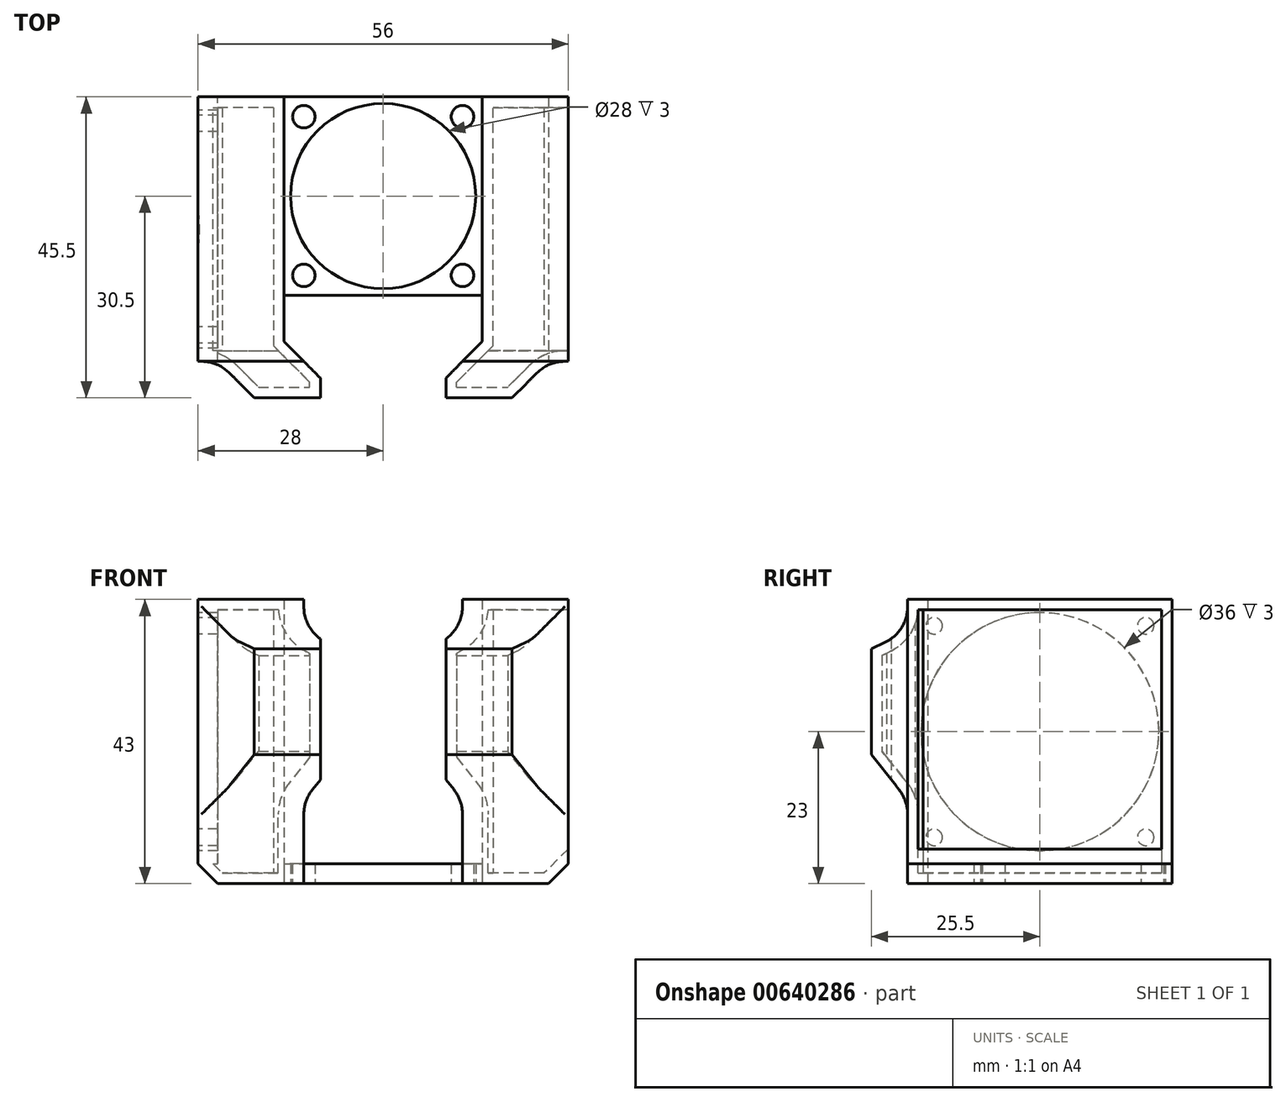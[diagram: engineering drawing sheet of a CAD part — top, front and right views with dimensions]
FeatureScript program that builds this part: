
annotation { "Feature Type Name" : "Feature", "Feature Type Description" : "" }
export const myFeature = defineFeature(function(context is Context, id is Id, definition is map)
    precondition{}
    {
        {
            var Q0;
            Q0=qCreatedBy(makeId("Top.planeOp"),FACE);
            var sketch = newSketch(context, id + "F0", { "sketchPlane" : qUnion([Q0])});
            skLineSegment(sketch, "E0", {"start": v(0, 0) * mm, "end": v(15, 0) * mm});
            skLineSegment(sketch, "E1", {"start": v(15, 0) * mm, "end": v(15, 30) * mm});
            skLineSegment(sketch, "E2", {"start": v(15, 30) * mm, "end": v(-15, 30) * mm});
            skLineSegment(sketch, "E3", {"start": v(-15, 30) * mm, "end": v(-15, 0) * mm});
            skLineSegment(sketch, "E4", {"start": v(-15, 0) * mm, "end": v(0, 0) * mm});
            skLineSegment(sketch, "E5", {"start": v(0, 0) * mm, "end": v(0, -15.5) * mm, "construction": true});
            skLineSegment(sketch, "E6", {"start": v(0, -15.5) * mm, "end": v(7, -15.5) * mm, "construction": true});
            skLineSegment(sketch, "E7", {"start": v(7, -15.5) * mm, "end": v(7, 0) * mm, "construction": true});
            skLineSegment(sketch, "E8", {"start": v(0, -15.5) * mm, "end": v(-7, -15.5) * mm, "construction": true});
            skLineSegment(sketch, "E9", {"start": v(-7, -15.5) * mm, "end": v(-7, 0) * mm, "construction": true});
            skLineSegment(sketch, "E10", {"start": v(-7, -15.5) * mm, "end": v(-47, -15.5) * mm, "construction": true});
            skLineSegment(sketch, "E11", {"start": v(7, -15.5) * mm, "end": v(47, -15.5) * mm, "construction": true});
            skLineSegment(sketch, "E12", {"start": v(-15, 30) * mm, "end": v(-15, -10) * mm, "construction": true});
            skLineSegment(sketch, "E13", {"start": v(15, 30) * mm, "end": v(15, -10) * mm, "construction": true});
            skLineSegment(sketch, "E14", {"start": v(-15, 30) * mm, "end": v(-25, 30) * mm});
            skLineSegment(sketch, "E15", {"start": v(-25, 30) * mm, "end": v(-25, -10) * mm, "construction": true});
            skLineSegment(sketch, "E16", {"start": v(-25, 30) * mm, "end": v(-28, 30) * mm});
            skLineSegment(sketch, "E17", {"start": v(-28, 30) * mm, "end": v(-28, -10) * mm});
            skLineSegment(sketch, "E18", {"start": v(-28, -10) * mm, "end": v(-25, -10) * mm});
            skLineSegment(sketch, "E19", {"start": v(-25, -10) * mm, "end": v(-19.5, -15.5) * mm});
            skLineSegment(sketch, "E20", {"start": v(-15, 0) * mm, "end": v(-15, -10) * mm});
            skLineSegment(sketch, "E21", {"start": v(-19.5, -15.5) * mm, "end": v(-9.5, -15.5) * mm});
            skLineSegment(sketch, "E22.MirrorCS", {"start": v(28, 30) * mm, "end": v(28, -10) * mm});
            skLineSegment(sketch, "E23.MirrorCS", {"start": v(28, -10) * mm, "end": v(25, -10) * mm});
            skLineSegment(sketch, "E24.MirrorCS", {"start": v(25, -10) * mm, "end": v(19.5, -15.5) * mm});
            skLineSegment(sketch, "E25.MirrorCS", {"start": v(15, 30) * mm, "end": v(25, 30) * mm});
            skLineSegment(sketch, "E26.MirrorCS", {"start": v(25, 30) * mm, "end": v(28, 30) * mm});
            skLineSegment(sketch, "E27", {"start": v(15, 0) * mm, "end": v(15, -10) * mm});
            skLineSegment(sketch, "E28", {"start": v(9.5, -15.5) * mm, "end": v(19.5, -15.5) * mm});
            skLineSegment(sketch, "E29", {"start": v(0, 30) * mm, "end": v(0, 0) * mm});
            skCircle(sketch, "E30", {"center": v(0, 15) * mm, "radius": 14 * mm});
            skLineSegment(sketch, "E31", {"start": v(-12, 27) * mm, "end": v(-12, 3) * mm, "construction": true});
            skLineSegment(sketch, "E32", {"start": v(-12, 3) * mm, "end": v(12, 3) * mm, "construction": true});
            skLineSegment(sketch, "E33", {"start": v(12, 3) * mm, "end": v(-12, 27) * mm, "construction": true});
            skLineSegment(sketch, "E34", {"start": v(-12, 27) * mm, "end": v(12, 27) * mm, "construction": true});
            skLineSegment(sketch, "E35", {"start": v(12, 27) * mm, "end": v(12, 3) * mm, "construction": true});
            skCircle(sketch, "E36", {"center": v(-12, 27) * mm, "radius": 1.7 * mm});
            skCircle(sketch, "E37", {"center": v(12, 27) * mm, "radius": 1.7 * mm});
            skCircle(sketch, "E38", {"center": v(12, 3) * mm, "radius": 1.7 * mm});
            skCircle(sketch, "E39", {"center": v(-12, 3) * mm, "radius": 1.7 * mm});
            skLineSegment(sketch, "E40", {"start": v(-9.5, -15.5) * mm, "end": v(-9.5, -12.5) * mm});
            skLineSegment(sketch, "E41", {"start": v(-9.5, -12.5) * mm, "end": v(-15, -7) * mm});
            skLineSegment(sketch, "E42.MirrorCS", {"start": v(9.5, -15.5) * mm, "end": v(9.5, -12.5) * mm});
            skLineSegment(sketch, "E43.MirrorCS", {"start": v(9.5, -12.5) * mm, "end": v(15, -7) * mm});
            skSolve(sketch);
        }
        {
            var Q0;
            {var subQ6=sQuery(id+"F0.wireOp",EDGE,"E3");Q0=makeQuery(id+"F0.imprint","IMPRINT",FACE,{"disambiguationData":[TD([[makeQuery(id+"F0.imprint","IMPRINT",EDGE,{"derivedFrom":subQ6}),1.0]])]});}
            var Q1;
            {var subQ5=sQuery(id+"F0.wireOp",EDGE,"E0");Q1=makeQuery(id+"F0.imprint","IMPRINT",FACE,{"disambiguationData":[TD([[makeQuery(id+"F0.imprint","IMPRINT",EDGE,{"derivedFrom":subQ5}),1.0]])]});}
            extrude(context, id + "F1", {"entities" : qUnion([Q0, Q1]), "depth" : 3 * mm, "offsetDistance" : 25 * mm});
        }
        {
            var Q0;
            Q0=makeQuery(id+"F0.imprint","IMPRINT",FACE,{"disambiguationData":[TD([[makeQuery(id+"F0.imprint","IMPRINT",EDGE,{"derivedFrom":sQuery(id+"F0.wireOp",EDGE,"E3")}),-1.0]])]});
            var Q1;
            Q1=makeQuery(id+"F0.imprint","IMPRINT",FACE,{"disambiguationData":[TD([[makeQuery(id+"F0.imprint","IMPRINT",EDGE,{"derivedFrom":sQuery(id+"F0.wireOp",EDGE,"E1")}),-1.0]])]});
            extrude(context, id + "F2", {"entities" : qUnion([Q0, Q1]), "operationType" : NewBodyOperationType.ADD, "depth" : 43 * mm, "offsetDistance" : 25 * mm});
        }
        {
            var Q0;
            Q0=qCreatedBy(makeId("Right.planeOp"),FACE);
            var sketch = newSketch(context, id + "F3", { "sketchPlane" : qUnion([Q0])});
            skLineSegment(sketch, "E44.0", {"start": v(-15.5, 19.5) * mm, "end": v(-15.5, 0) * mm});
            skLineSegment(sketch, "E45", {"start": v(-10, 12.58) * mm, "end": v(-15.5, 19.5) * mm});
            skLineSegment(sketch, "E46", {"start": v(0, 0) * mm, "end": v(-15.5, 0) * mm});
            skPoint(sketch, "E47.orphan", {"position": v(-15.5, 43) * mm});
            skLineSegment(sketch, "E48", {"start": v(-15.5, 43) * mm, "end": v(-15.5, 27.5) * mm});
            skLineSegment(sketch, "E49", {"start": v(-15.5, 43) * mm, "end": v(0, 43) * mm});
            skLineSegment(sketch, "E50", {"start": v(-10, 38.16) * mm, "end": v(-15.5, 35.5) * mm});
            skLineSegment(sketch, "E51.0", {"start": v(-10, 43) * mm, "end": v(-10, 0) * mm});
            skSolve(sketch);
        }
        {
            var Q0;
            Q0 = qSketchRegion(id + "F3", true);
            extrude(context, id + "F4", {"entities" : qUnion([Q0]), "operationType" : NewBodyOperationType.REMOVE, "oppositeDirection" : true, "depth" : 25 * mm, "offsetDistance" : 25 * mm, "hasSecondDirection" : true, "secondDirectionOppositeDirection" : false, "secondDirectionDepth" : 25 * mm});
        }
        {
            var Q0;
            {var subQ0=sQuery(id+"F3.wireOp",EDGE,"E50");var subQ1=sQuery(id+"F3.wireOp",EDGE,"E51.0");Q0=makeQuery(id+"F4.boolean.opBoolean","COPY",EDGE,{"disambiguationData":[topologyDisambiguationEdgeConnected([makeQuery(id+"F2.opExtrude","SWEPT_FACE",FACE,{"disambiguationData":[OSD([sQuery(id+"F0.wireOp",EDGE,"E18")])]})])],"derivedFrom":makeQuery(id+"F4.opExtrude","SWEPT_EDGE",EDGE,{"disambiguationData":[OSD([subQ0,subQ1])]})});}
            var Q1;
            Q1=makeQuery(id+"F2.opExtrude","SWEPT_EDGE",EDGE,{"disambiguationData":[OSD([sQuery(id+"F0.wireOp",EDGE,"E18"),sQuery(id+"F0.wireOp",EDGE,"E19")])]});
            var Q2;
            {var subQ0=sQuery(id+"F3.wireOp",EDGE,"E45");var subQ1=sQuery(id+"F3.wireOp",EDGE,"E51.0");Q2=makeQuery(id+"F4.boolean.opBoolean","COPY",EDGE,{"disambiguationData":[topologyDisambiguationEdgeConnected([makeQuery(id+"F2.opExtrude","SWEPT_FACE",FACE,{"disambiguationData":[OSD([sQuery(id+"F0.wireOp",EDGE,"E18")])]})])],"derivedFrom":makeQuery(id+"F4.opExtrude","SWEPT_EDGE",EDGE,{"disambiguationData":[OSD([subQ0,subQ1])]})});}
            var Q3;
            {var subQ0=sQuery(id+"F3.wireOp",EDGE,"E45");var subQ1=sQuery(id+"F3.wireOp",EDGE,"E51.0");Q3=makeQuery(id+"F4.boolean.opBoolean","COPY",EDGE,{"disambiguationData":[topologyDisambiguationEdgeConnected([makeQuery(id+"F2.opExtrude","SWEPT_FACE",FACE,{"disambiguationData":[OSD([sQuery(id+"F0.wireOp",EDGE,"E23.MirrorCS")])]})])],"derivedFrom":makeQuery(id+"F4.opExtrude","SWEPT_EDGE",EDGE,{"disambiguationData":[OSD([subQ0,subQ1])]})});}
            var Q4;
            Q4=makeQuery(id+"F2.opExtrude","SWEPT_EDGE",EDGE,{"disambiguationData":[OSD([sQuery(id+"F0.wireOp",EDGE,"E23.MirrorCS"),sQuery(id+"F0.wireOp",EDGE,"E24.MirrorCS")])]});
            var Q5;
            {var subQ0=sQuery(id+"F3.wireOp",EDGE,"E50");var subQ1=sQuery(id+"F3.wireOp",EDGE,"E51.0");Q5=makeQuery(id+"F4.boolean.opBoolean","COPY",EDGE,{"disambiguationData":[topologyDisambiguationEdgeConnected([makeQuery(id+"F2.opExtrude","SWEPT_FACE",FACE,{"disambiguationData":[OSD([sQuery(id+"F0.wireOp",EDGE,"E23.MirrorCS")])]})])],"derivedFrom":makeQuery(id+"F4.opExtrude","SWEPT_EDGE",EDGE,{"disambiguationData":[OSD([subQ0,subQ1])]})});}
            fillet(context, id + "F5", {"entities" : qUnion([Q0, Q1, Q2, Q3, Q4, Q5]), "radius" : 6 * mm, "tangentPropagation" : true, "allowEdgeOverflow" : false});
        }
        {
            var Q0;
            Q0=makeQuery(id+"F2.opExtrude","CAP_EDGE",EDGE,{"disambiguationData":[OSD([sQuery(id+"F0.wireOp",EDGE,"E22.MirrorCS")])],"isStart":true});
            var Q1;
            Q1=makeQuery(id+"F2.opExtrude","CAP_EDGE",EDGE,{"disambiguationData":[OSD([sQuery(id+"F0.wireOp",EDGE,"E17")])],"isStart":true});
            chamfer(context, id + "F6", {"entities" : qUnion([Q0, Q1]), "width" : 3 * mm, "tangentPropagation" : true});
        }
        {
            var Q0;
            Q0=makeQuery(id+"F2.opExtrude","SWEPT_FACE",FACE,{"disambiguationData":[OSD([sQuery(id+"F0.wireOp",EDGE,"E17")])]});
            var Q1;
            Q1=makeQuery(id+"F2.opExtrude","SWEPT_FACE",FACE,{"disambiguationData":[OSD([sQuery(id+"F0.wireOp",EDGE,"E22.MirrorCS")])]});
            shell(context, id + "F7", {"entities" : qUnion([Q0, Q1]), "thickness" : 1.6 * mm});
        }
        {
            var Q0;
            Q0=makeQuery(id+"F2.opExtrude","SWEPT_FACE",FACE,{"disambiguationData":[OSD([sQuery(id+"F0.wireOp",EDGE,"E17")])]});
            var sketch = newSketch(context, id + "F8", { "sketchPlane" : qUnion([Q0])});
            skLineSegment(sketch, "E52.0", {"start": v(-30, 43) * mm, "end": v(10, 43) * mm});
            skLineSegment(sketch, "E52.1", {"start": v(-30, 43) * mm, "end": v(-30, 0) * mm});
            skLineSegment(sketch, "E52.2", {"start": v(10, 43) * mm, "end": v(10, 0) * mm});
            skLineSegment(sketch, "E53", {"start": v(-26, 39) * mm, "end": v(-26, 7) * mm, "construction": true});
            skLineSegment(sketch, "E54", {"start": v(-26, 7) * mm, "end": v(6, 7) * mm, "construction": true});
            skLineSegment(sketch, "E55", {"start": v(6, 7) * mm, "end": v(6, 39) * mm, "construction": true});
            skLineSegment(sketch, "E56", {"start": v(6, 39) * mm, "end": v(-26, 39) * mm, "construction": true});
            skLineSegment(sketch, "E57", {"start": v(6, 7) * mm, "end": v(-26, 39) * mm, "construction": true});
            skLineSegment(sketch, "E58.0", {"start": v(-30, 3) * mm, "end": v(10, 3) * mm});
            skLineSegment(sketch, "E59", {"start": v(10, 3) * mm, "end": v(-30, 43) * mm, "construction": true});
            skCircle(sketch, "E60", {"center": v(-26, 39) * mm, "radius": 1.25 * mm});
            skCircle(sketch, "E61", {"center": v(6, 39) * mm, "radius": 1.25 * mm});
            skCircle(sketch, "E62", {"center": v(-26, 7) * mm, "radius": 1.25 * mm});
            skCircle(sketch, "E63", {"center": v(6, 7) * mm, "radius": 1.25 * mm});
            skCircle(sketch, "E64", {"center": v(-10, 23) * mm, "radius": 18 * mm});
            skSolve(sketch);
        }
        {
            var Q0;
            Q0 = qSketchRegion(id + "F8", true);
            var Q1;
            {var subQ1=sQuery(id+"F0.wireOp",EDGE,"E17");var subQ6=makeQuery(id+"F7.opShell","OFFSET_EDGE",EDGE,{"disambiguationData":[OSD([subQ1]),TDD([makeQuery(id+"F2.opExtrude","CAP_EDGE",EDGE,{"disambiguationData":[OSD([subQ1])],"isStart":true})])]});Q1=makeQuery(id+"F8.imprint","IMPRINT",FACE,{"disambiguationData":[TD([[makeQuery(id+"F8.imprint","IMPRINT",EDGE,{"derivedFrom":subQ6}),1.0]])]});}
            extrude(context, id + "F9", {"entities" : qUnion([Q0, Q1]), "operationType" : NewBodyOperationType.ADD, "oppositeDirection" : true, "depth" : 3 * mm, "offsetDistance" : 25 * mm});
        }
    });
